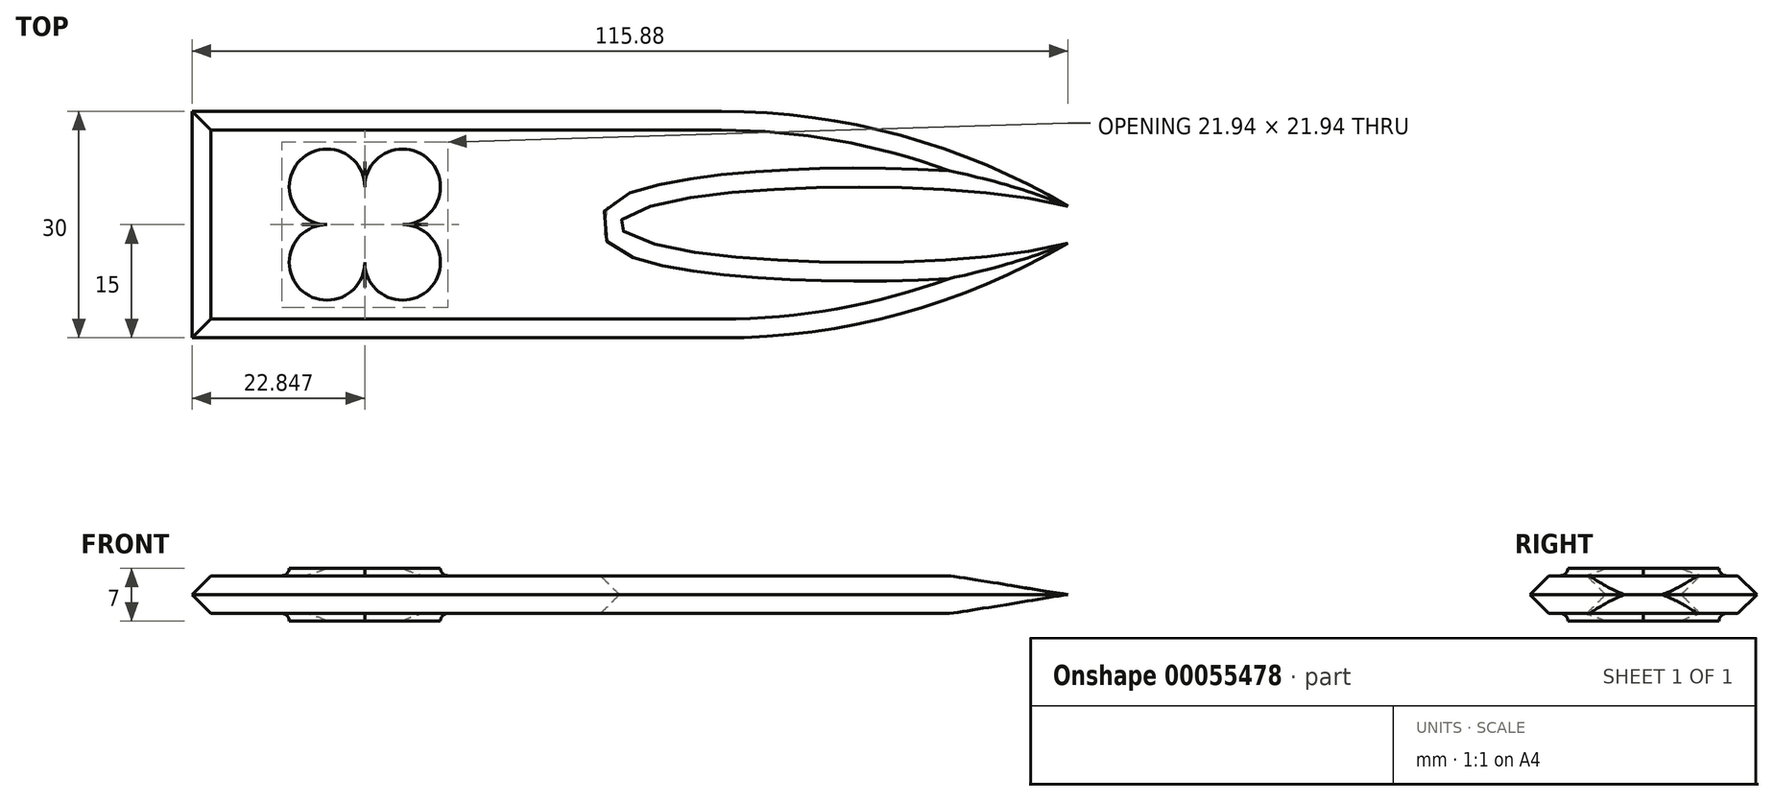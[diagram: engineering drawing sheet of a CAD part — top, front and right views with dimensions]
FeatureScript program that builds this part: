
annotation { "Feature Type Name" : "Feature", "Feature Type Description" : "" }
export const myFeature = defineFeature(function(context is Context, id is Id, definition is map)
    precondition{}
    {
        {
            var Q0;
            Q0=qCreatedBy(makeId("Top.planeOp"),FACE);
            var sketch = newSketch(context, id + "F0", { "sketchPlane" : qUnion([Q0])});
            skEllipticalArc(sketch, "E0", {});
            skArc(sketch, "E1", {"start": v(59.34, 2.43) * mm, "mid": v(37.25, 11.8) * mm, "end": v(13.46, 15) * mm});
            skLineSegment(sketch, "E2", {"start": v(13.46, 15) * mm, "end": v(-56.54, 15) * mm});
            skLineSegment(sketch, "E3", {"start": v(-56.54, 15) * mm, "end": v(-56.54, 0) * mm});
            skLineSegment(sketch, "E4", {"start": v(-56.54, 0) * mm, "end": v(0, 0) * mm});
            skArc(sketch, "E5.MirrorCS", {"start": v(59.34, -2.43) * mm, "mid": v(37.25, -11.8) * mm, "end": v(13.46, -15) * mm});
            skLineSegment(sketch, "E6.MirrorCS", {"start": v(13.46, -15) * mm, "end": v(-56.54, -15) * mm});
            skEllipticalArc(sketch, "E7.MirrorCS", {});
            skLineSegment(sketch, "E8.MirrorCS", {"start": v(-56.54, -15) * mm, "end": v(-56.54, 0) * mm});
            skLineSegment(sketch, "E9", {"start": v(-56.54, 7.5) * mm, "end": v(-106.54, 7.5) * mm});
            skLineSegment(sketch, "E10", {"start": v(-106.54, 7.5) * mm, "end": v(-106.54, 0) * mm});
            skPoint(sketch, "E10.endSnap0", {"position": v(-56.54, -7.5) * mm});
            skLineSegment(sketch, "E11", {"start": v(-56.54, 15) * mm, "end": v(-56.54, 19.5) * mm});
            skLineSegment(sketch, "E12", {"start": v(-56.54, 19.5) * mm, "end": v(-61.54, 19.5) * mm});
            skLineSegment(sketch, "E13", {"start": v(-61.54, 19.5) * mm, "end": v(-61.54, 7.5) * mm});
            skLineSegment(sketch, "E14", {"start": v(-56.54, 0) * mm, "end": v(-106.54, 0) * mm});
            skPoint(sketch, "E15.orphan", {"position": v(-106.54, -7.5) * mm});
            const initialGuessF0  = {"E0": [0.031665493547578756, 0, -1, 0, 0.03166549354757875, 0.005, 3.6489930299235205, 0], "E7.MirrorCS": [0.031665493547578756, 0, -1, 0, 0.03166549354757875, 0.005, 0, 2.6341922772560658]};
            skSetInitialGuess(sketch, initialGuessF0);
            skSolve(sketch);
        }
        {
            var Q0;
            Q0=makeQuery(id+"F0.imprint","IMPRINT",FACE,{"disambiguationData":[TD([[makeQuery(id+"F0.imprint","IMPRINT",EDGE,{"derivedFrom":sQuery(id+"F0.wireOp",EDGE,"E0")}),-1.0]])]});
            var Q1;
            Q1=makeQuery(id+"F0.imprint","IMPRINT",FACE,{"disambiguationData":[TD([[makeQuery(id+"F0.imprint","IMPRINT",EDGE,{"derivedFrom":sQuery(id+"F0.wireOp",EDGE,"E4")}),-1.0]])]});
            extrude(context, id + "F1", {"entities" : qUnion([Q0, Q1]), "endBound" : BoundingType.SYMMETRIC, "depth" : 5 * mm});
        }
        {
            var Q0;
            Q0=makeQuery(id+"F1.opExtrude","CAP_FACE",FACE,{"disambiguationData":[OSD([sQuery(id+"F0.wireOp",EDGE,"E0"),sQuery(id+"F0.wireOp",EDGE,"E1"),sQuery(id+"F0.wireOp",EDGE,"E2"),sQuery(id+"F0.wireOp",EDGE,"E3"),sQuery(id+"F0.wireOp",EDGE,"E5.MirrorCS"),sQuery(id+"F0.wireOp",EDGE,"E6.MirrorCS"),sQuery(id+"F0.wireOp",EDGE,"E7.MirrorCS"),sQuery(id+"F0.wireOp",EDGE,"E8.MirrorCS")])],"isStart":false});
            var Q1;
            Q1=makeQuery(id+"F1.opExtrude","CAP_FACE",FACE,{"disambiguationData":[OSD([sQuery(id+"F0.wireOp",EDGE,"E0"),sQuery(id+"F0.wireOp",EDGE,"E1"),sQuery(id+"F0.wireOp",EDGE,"E2"),sQuery(id+"F0.wireOp",EDGE,"E3"),sQuery(id+"F0.wireOp",EDGE,"E5.MirrorCS"),sQuery(id+"F0.wireOp",EDGE,"E6.MirrorCS"),sQuery(id+"F0.wireOp",EDGE,"E7.MirrorCS"),sQuery(id+"F0.wireOp",EDGE,"E8.MirrorCS")])],"isStart":true});
            chamfer(context, id + "F2", {"entities" : qUnion([Q0, Q1]), "width" : 2.5 * mm, "tangentPropagation" : true});
        }
        {
            var Q0;
            Q0=qCreatedBy(makeId("Top.planeOp"),FACE);
            var sketch = newSketch(context, id + "F3", { "sketchPlane" : qUnion([Q0])});
            skLineSegment(sketch, "E16.0", {"start": v(-28.7, -5) * mm, "end": v(-38.7, -5) * mm, "construction": true});
            skLineSegment(sketch, "E16.1", {"start": v(-38.7, -5) * mm, "end": v(-38.7, 5) * mm, "construction": true});
            skLineSegment(sketch, "E16.2", {"start": v(-38.7, 5) * mm, "end": v(-28.7, 5) * mm, "construction": true});
            skLineSegment(sketch, "E16.3", {"start": v(-28.7, 5) * mm, "end": v(-28.7, -5) * mm, "construction": true});
            skPoint(sketch, "E16.0.midPoint", {"position": v(-33.7, -5) * mm});
            skArc(sketch, "E17", {"start": v(-28.7, 0) * mm, "mid": v(-25.16, 8.54) * mm, "end": v(-33.7, 5) * mm});
            skArc(sketch, "E18", {"start": v(-33.7, 5) * mm, "mid": v(-42.23, 8.54) * mm, "end": v(-38.7, 0) * mm});
            skArc(sketch, "E19", {"start": v(-38.7, 0) * mm, "mid": v(-42.23, -8.54) * mm, "end": v(-33.7, -5) * mm});
            skArc(sketch, "E20", {"start": v(-33.7, -5) * mm, "mid": v(-25.16, -8.54) * mm, "end": v(-28.7, 0) * mm});
            skPoint(sketch, "E21", {"position": v(-33.7, 0) * mm});
            skSolve(sketch);
        }
        {
            var Q0;
            Q0 = qSketchRegion(id + "F3", true);
            extrude(context, id + "F4", {"entities" : qUnion([Q0]), "operationType" : NewBodyOperationType.ADD, "endBound" : BoundingType.SYMMETRIC, "depth" : 7 * mm});
        }
        {
            var Q0;
            Q0=makeQuery(id+"F4.boolean.opBoolean","INTERSECT",EDGE,{"derivedFrom":[makeQuery(id+"F1.opExtrude","CAP_FACE",FACE,{"disambiguationData":[OSD([sQuery(id+"F0.wireOp",EDGE,"E0"),sQuery(id+"F0.wireOp",EDGE,"E1"),sQuery(id+"F0.wireOp",EDGE,"E2"),sQuery(id+"F0.wireOp",EDGE,"E3"),sQuery(id+"F0.wireOp",EDGE,"E5.MirrorCS"),sQuery(id+"F0.wireOp",EDGE,"E6.MirrorCS"),sQuery(id+"F0.wireOp",EDGE,"E7.MirrorCS"),sQuery(id+"F0.wireOp",EDGE,"E8.MirrorCS")])],"isStart":false}),makeQuery(id+"F4.opExtrude","SWEPT_FACE",FACE,{"disambiguationData":[OSD([sQuery(id+"F3.wireOp",EDGE,"E19")])]})]});
            var Q1;
            Q1=makeQuery(id+"F4.boolean.opBoolean","INTERSECT",EDGE,{"derivedFrom":[makeQuery(id+"F1.opExtrude","CAP_FACE",FACE,{"disambiguationData":[OSD([sQuery(id+"F0.wireOp",EDGE,"E0"),sQuery(id+"F0.wireOp",EDGE,"E1"),sQuery(id+"F0.wireOp",EDGE,"E2"),sQuery(id+"F0.wireOp",EDGE,"E3"),sQuery(id+"F0.wireOp",EDGE,"E5.MirrorCS"),sQuery(id+"F0.wireOp",EDGE,"E6.MirrorCS"),sQuery(id+"F0.wireOp",EDGE,"E7.MirrorCS"),sQuery(id+"F0.wireOp",EDGE,"E8.MirrorCS")])],"isStart":false}),makeQuery(id+"F4.opExtrude","SWEPT_FACE",FACE,{"disambiguationData":[OSD([sQuery(id+"F3.wireOp",EDGE,"E18")])]})]});
            var Q2;
            Q2=makeQuery(id+"F4.boolean.opBoolean","INTERSECT",EDGE,{"derivedFrom":[makeQuery(id+"F1.opExtrude","CAP_FACE",FACE,{"disambiguationData":[OSD([sQuery(id+"F0.wireOp",EDGE,"E0"),sQuery(id+"F0.wireOp",EDGE,"E1"),sQuery(id+"F0.wireOp",EDGE,"E2"),sQuery(id+"F0.wireOp",EDGE,"E3"),sQuery(id+"F0.wireOp",EDGE,"E5.MirrorCS"),sQuery(id+"F0.wireOp",EDGE,"E6.MirrorCS"),sQuery(id+"F0.wireOp",EDGE,"E7.MirrorCS"),sQuery(id+"F0.wireOp",EDGE,"E8.MirrorCS")])],"isStart":false}),makeQuery(id+"F4.opExtrude","SWEPT_FACE",FACE,{"disambiguationData":[OSD([sQuery(id+"F3.wireOp",EDGE,"E17")])]})]});
            var Q3;
            Q3=makeQuery(id+"F4.boolean.opBoolean","INTERSECT",EDGE,{"derivedFrom":[makeQuery(id+"F1.opExtrude","CAP_FACE",FACE,{"disambiguationData":[OSD([sQuery(id+"F0.wireOp",EDGE,"E0"),sQuery(id+"F0.wireOp",EDGE,"E1"),sQuery(id+"F0.wireOp",EDGE,"E2"),sQuery(id+"F0.wireOp",EDGE,"E3"),sQuery(id+"F0.wireOp",EDGE,"E5.MirrorCS"),sQuery(id+"F0.wireOp",EDGE,"E6.MirrorCS"),sQuery(id+"F0.wireOp",EDGE,"E7.MirrorCS"),sQuery(id+"F0.wireOp",EDGE,"E8.MirrorCS")])],"isStart":false}),makeQuery(id+"F4.opExtrude","SWEPT_FACE",FACE,{"disambiguationData":[OSD([sQuery(id+"F3.wireOp",EDGE,"E20")])]})]});
            var Q4;
            Q4=makeQuery(id+"F4.boolean.opBoolean","INTERSECT",EDGE,{"derivedFrom":[makeQuery(id+"F1.opExtrude","CAP_FACE",FACE,{"disambiguationData":[OSD([sQuery(id+"F0.wireOp",EDGE,"E0"),sQuery(id+"F0.wireOp",EDGE,"E1"),sQuery(id+"F0.wireOp",EDGE,"E2"),sQuery(id+"F0.wireOp",EDGE,"E3"),sQuery(id+"F0.wireOp",EDGE,"E5.MirrorCS"),sQuery(id+"F0.wireOp",EDGE,"E6.MirrorCS"),sQuery(id+"F0.wireOp",EDGE,"E7.MirrorCS"),sQuery(id+"F0.wireOp",EDGE,"E8.MirrorCS")])],"isStart":true}),makeQuery(id+"F4.opExtrude","SWEPT_FACE",FACE,{"disambiguationData":[OSD([sQuery(id+"F3.wireOp",EDGE,"E18")])]})]});
            var Q5;
            Q5=makeQuery(id+"F4.boolean.opBoolean","INTERSECT",EDGE,{"derivedFrom":[makeQuery(id+"F1.opExtrude","CAP_FACE",FACE,{"disambiguationData":[OSD([sQuery(id+"F0.wireOp",EDGE,"E0"),sQuery(id+"F0.wireOp",EDGE,"E1"),sQuery(id+"F0.wireOp",EDGE,"E2"),sQuery(id+"F0.wireOp",EDGE,"E3"),sQuery(id+"F0.wireOp",EDGE,"E5.MirrorCS"),sQuery(id+"F0.wireOp",EDGE,"E6.MirrorCS"),sQuery(id+"F0.wireOp",EDGE,"E7.MirrorCS"),sQuery(id+"F0.wireOp",EDGE,"E8.MirrorCS")])],"isStart":true}),makeQuery(id+"F4.opExtrude","SWEPT_FACE",FACE,{"disambiguationData":[OSD([sQuery(id+"F3.wireOp",EDGE,"E17")])]})]});
            var Q6;
            Q6=makeQuery(id+"F4.boolean.opBoolean","INTERSECT",EDGE,{"derivedFrom":[makeQuery(id+"F1.opExtrude","CAP_FACE",FACE,{"disambiguationData":[OSD([sQuery(id+"F0.wireOp",EDGE,"E0"),sQuery(id+"F0.wireOp",EDGE,"E1"),sQuery(id+"F0.wireOp",EDGE,"E2"),sQuery(id+"F0.wireOp",EDGE,"E3"),sQuery(id+"F0.wireOp",EDGE,"E5.MirrorCS"),sQuery(id+"F0.wireOp",EDGE,"E6.MirrorCS"),sQuery(id+"F0.wireOp",EDGE,"E7.MirrorCS"),sQuery(id+"F0.wireOp",EDGE,"E8.MirrorCS")])],"isStart":true}),makeQuery(id+"F4.opExtrude","SWEPT_FACE",FACE,{"disambiguationData":[OSD([sQuery(id+"F3.wireOp",EDGE,"E20")])]})]});
            var Q7;
            Q7=makeQuery(id+"F4.boolean.opBoolean","INTERSECT",EDGE,{"derivedFrom":[makeQuery(id+"F1.opExtrude","CAP_FACE",FACE,{"disambiguationData":[OSD([sQuery(id+"F0.wireOp",EDGE,"E0"),sQuery(id+"F0.wireOp",EDGE,"E1"),sQuery(id+"F0.wireOp",EDGE,"E2"),sQuery(id+"F0.wireOp",EDGE,"E3"),sQuery(id+"F0.wireOp",EDGE,"E5.MirrorCS"),sQuery(id+"F0.wireOp",EDGE,"E6.MirrorCS"),sQuery(id+"F0.wireOp",EDGE,"E7.MirrorCS"),sQuery(id+"F0.wireOp",EDGE,"E8.MirrorCS")])],"isStart":true}),makeQuery(id+"F4.opExtrude","SWEPT_FACE",FACE,{"disambiguationData":[OSD([sQuery(id+"F3.wireOp",EDGE,"E19")])]})]});
            fillet(context, id + "F5", {"entities" : qUnion([Q0, Q1, Q2, Q3, Q4, Q5, Q6, Q7]), "radius" : 1 * mm, "tangentPropagation" : true, "allowEdgeOverflow" : false});
        }
    });
